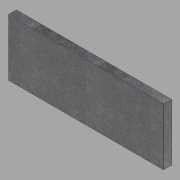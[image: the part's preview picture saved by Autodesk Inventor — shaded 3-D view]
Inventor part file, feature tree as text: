
AUTODESK INVENTOR PART (.ipt)
format: ipt  version: 2022.1 (Build 261234020, 234B)  size: 112,640 bytes
history: native  units: in
note: dims shown in document units (in); Inventor stores cm internally (conversion verified against a paired STEP export)
features: extrude x1, fillet x1, sketch x1
ambient origin geometry x8: Origin, YZ Plane, XZ Plane, XY Plane, X Axis, Y Axis, Z Axis, Center Point
bodies: Solid1 (feature_tree)
feature tree (3):
  extrude  "Extrusion1"  Depth=42.0in
  fillet  "Fillet1"  Radius=6.0in
  sketch  "Sketch1"  dims[d0=114.0in d1=42.0in d2=6.0in d3=0.0in d4=0.25in]
